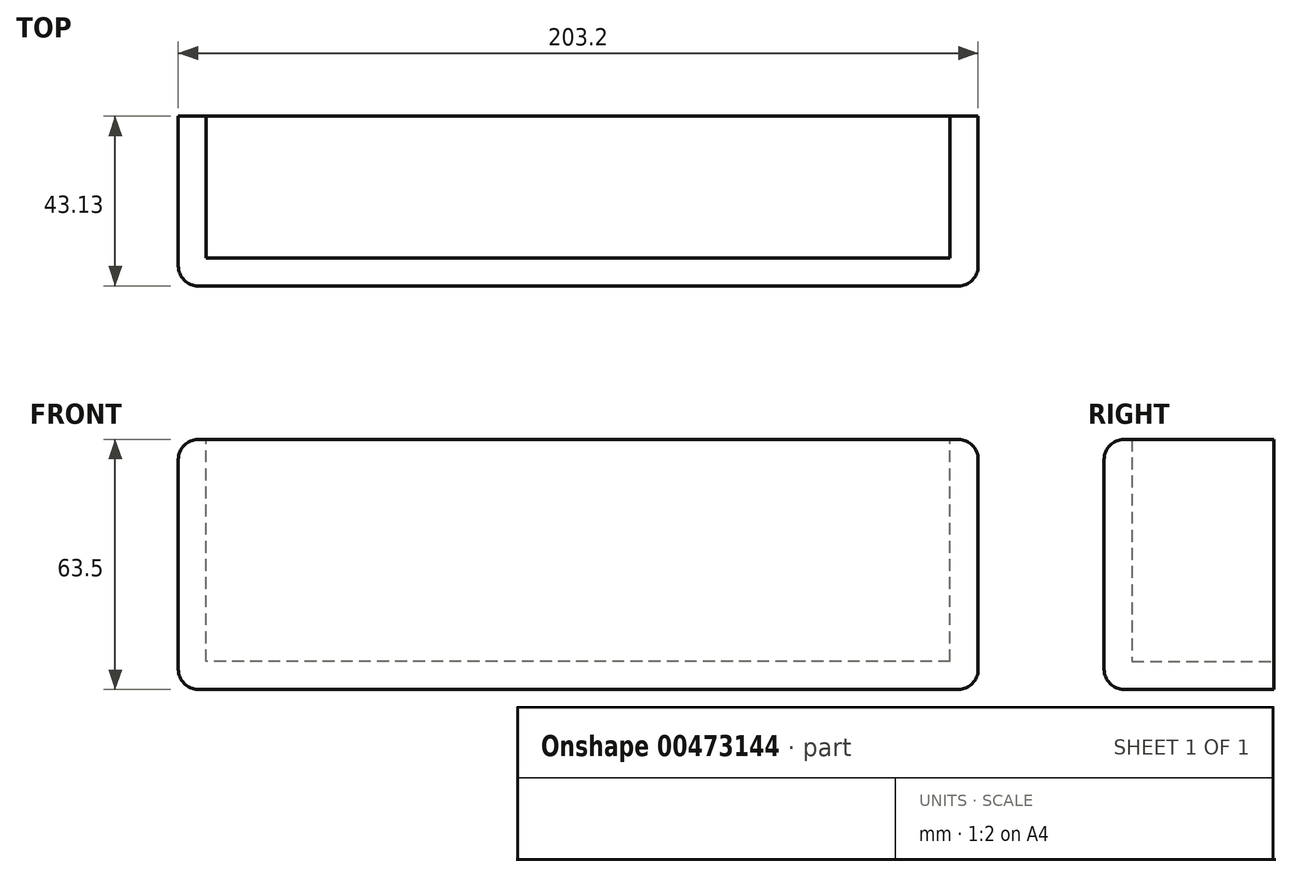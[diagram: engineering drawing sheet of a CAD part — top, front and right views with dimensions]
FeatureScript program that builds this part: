
annotation { "Feature Type Name" : "Feature", "Feature Type Description" : "" }
export const myFeature = defineFeature(function(context is Context, id is Id, definition is map)
    precondition{}
    {
        {
            var Q0;
            Q0=qCreatedBy(makeId("Front.planeOp"),FACE);
            var sketch = newSketch(context, id + "F0", { "sketchPlane" : qUnion([Q0])});
            skLineSegment(sketch, "E0.bottom", {"start": v(-101.8, 0.92) * mm, "end": v(101.4, 0.92) * mm});
            skLineSegment(sketch, "E0.top", {"start": v(-101.8, -62.58) * mm, "end": v(101.4, -62.58) * mm});
            skLineSegment(sketch, "E0.left", {"start": v(-101.8, 0.92) * mm, "end": v(-101.8, -62.58) * mm});
            skLineSegment(sketch, "E0.right", {"start": v(101.4, 0.92) * mm, "end": v(101.4, -62.58) * mm});
            skPoint(sketch, "E1", {"position": v(39.42, -31.28) * mm});
            skPoint(sketch, "E2", {"position": v(-36.78, -31.17) * mm});
            skSolve(sketch);
        }
        {
            var Q0;
            Q0=makeQuery(id+"F0.imprint","IMPRINT",FACE,{"disambiguationData":[TD([[makeQuery(id+"F0.imprint","IMPRINT",EDGE,{"derivedFrom":sQuery(id+"F0.wireOp",EDGE,"E0.bottom")}),-1.0]])]});
            extrude(context, id + "F1", {"entities" : qUnion([Q0]), "depth" : 50.8 * mm});
        }
        {
            var Q0;
            Q0=makeQuery(id+"F1.opExtrude","SWEPT_FACE",FACE,{"disambiguationData":[OSD([sQuery(id+"F0.wireOp",EDGE,"E0.bottom")])]});
            shell(context, id + "F2", {"entities" : qUnion([Q0]), "thickness" : 7.11 * mm});
        }
        {
            var Q0;
            Q0=makeQuery(id+"F1.opExtrude","SWEPT_FACE",FACE,{"disambiguationData":[OSD([sQuery(id+"F0.wireOp",EDGE,"E0.left")])]});
            var sketch = newSketch(context, id + "F3", { "sketchPlane" : qUnion([Q0])});
            skLineSegment(sketch, "E3.bottom", {"start": v(0, 0.92) * mm, "end": v(7.67, 0.92) * mm});
            skLineSegment(sketch, "E3.top", {"start": v(0, -62.58) * mm, "end": v(7.67, -62.58) * mm});
            skLineSegment(sketch, "E3.left", {"start": v(0, 0.92) * mm, "end": v(0, -62.58) * mm});
            skLineSegment(sketch, "E3.right", {"start": v(7.67, 0.92) * mm, "end": v(7.67, -62.58) * mm});
            skSolve(sketch);
        }
        {
            var Q0;
            Q0=makeQuery(id+"F3.imprint","IMPRINT",FACE,{"disambiguationData":[TD([[makeQuery(id+"F3.imprint","IMPRINT",EDGE,{"derivedFrom":sQuery(id+"F3.wireOp",EDGE,"E3.bottom")}),1.0]])]});
            extrude(context, id + "F4", {"entities" : qUnion([Q0]), "operationType" : NewBodyOperationType.REMOVE, "oppositeDirection" : true, "depth" : 208.03 * mm});
        }
        {
            var Q0;
            Q0=makeQuery(id+"F1.opExtrude","SWEPT_EDGE",EDGE,{"disambiguationData":[OSD([sQuery(id+"F0.wireOp",EDGE,"E0.bottom"),sQuery(id+"F0.wireOp",EDGE,"E0.left")])]});
            var Q1;
            Q1=makeQuery(id+"F1.opExtrude","CAP_EDGE",EDGE,{"disambiguationData":[OSD([sQuery(id+"F0.wireOp",EDGE,"E0.bottom")])],"isStart":false});
            var Q2;
            Q2=makeQuery(id+"F1.opExtrude","CAP_EDGE",EDGE,{"disambiguationData":[OSD([sQuery(id+"F0.wireOp",EDGE,"E0.left")])],"isStart":false});
            var Q3;
            Q3=makeQuery(id+"F1.opExtrude","SWEPT_EDGE",EDGE,{"disambiguationData":[OSD([sQuery(id+"F0.wireOp",EDGE,"E0.top"),sQuery(id+"F0.wireOp",EDGE,"E0.left")])]});
            var Q4;
            Q4=makeQuery(id+"F1.opExtrude","CAP_EDGE",EDGE,{"disambiguationData":[OSD([sQuery(id+"F0.wireOp",EDGE,"E0.top")])],"isStart":false});
            var Q5;
            Q5=makeQuery(id+"F1.opExtrude","SWEPT_EDGE",EDGE,{"disambiguationData":[OSD([sQuery(id+"F0.wireOp",EDGE,"E0.top"),sQuery(id+"F0.wireOp",EDGE,"E0.right")])]});
            var Q6;
            Q6=makeQuery(id+"F1.opExtrude","CAP_EDGE",EDGE,{"disambiguationData":[OSD([sQuery(id+"F0.wireOp",EDGE,"E0.right")])],"isStart":false});
            var Q7;
            Q7=makeQuery(id+"F1.opExtrude","SWEPT_EDGE",EDGE,{"disambiguationData":[OSD([sQuery(id+"F0.wireOp",EDGE,"E0.bottom"),sQuery(id+"F0.wireOp",EDGE,"E0.right")])]});
            fillet(context, id + "F5", {"entities" : qUnion([Q0, Q1, Q2, Q3, Q4, Q5, Q6, Q7]), "radius" : 5.08 * mm, "tangentPropagation" : true, "allowEdgeOverflow" : false});
        }
    });
